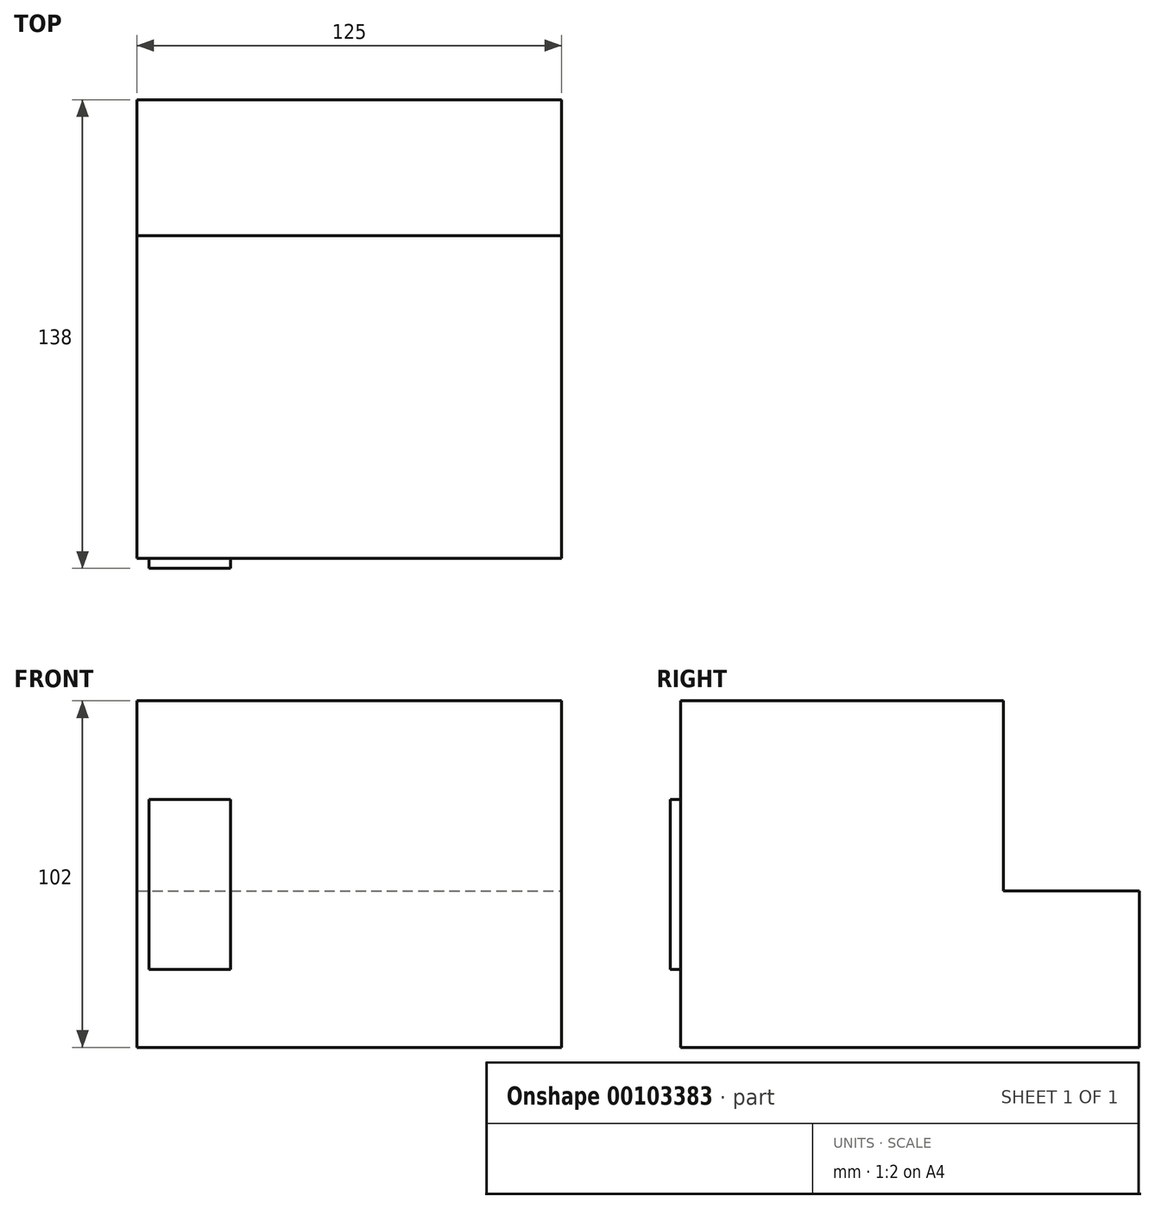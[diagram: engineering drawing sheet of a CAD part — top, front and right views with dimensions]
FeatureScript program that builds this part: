
annotation { "Feature Type Name" : "Feature", "Feature Type Description" : "" }
export const myFeature = defineFeature(function(context is Context, id is Id, definition is map)
    precondition{}
    {
        {
            var Q0;
            Q0=qCreatedBy(makeId("Top.planeOp"),FACE);
            var sketch = newSketch(context, id + "F0", { "sketchPlane" : qUnion([Q0])});
            skLineSegment(sketch, "E0.bottom", {"start": v(0, 0) * mm, "end": v(125, 0) * mm});
            skLineSegment(sketch, "E0.top", {"start": v(0, 135) * mm, "end": v(125, 135) * mm});
            skLineSegment(sketch, "E0.left", {"start": v(0, 0) * mm, "end": v(0, 135) * mm});
            skLineSegment(sketch, "E0.right", {"start": v(125, 0) * mm, "end": v(125, 135) * mm});
            skLineSegment(sketch, "E1", {"start": v(0, 95) * mm, "end": v(125, 95) * mm});
            skSolve(sketch);
        }
        {
            var Q0;
            Q0=qSketchRegion(id+"F0",true);
            var Q1;
            Q1=makeQuery(id+"F0.imprint","IMPRINT",FACE,{"disambiguationData":[TD([[makeQuery(id+"F0.imprint","IMPRINT",EDGE,{"derivedFrom":sQuery(id+"F0.wireOp",EDGE,"E0.bottom")}),1.0]])]});
            extrude(context, id + "F1", {"entities" : qUnion([Q0, Q1]), "depth" : 102 * mm});
        }
        {
            var Q0;
            {var subQ0=sQuery(id+"F0.wireOp",EDGE,"E0.top");Q0=makeQuery(id+"F0.imprint","IMPRINT",FACE,{"disambiguationData":[TD([[makeQuery(id+"F0.imprint","IMPRINT",EDGE,{"derivedFrom":subQ0}),-1.0]])]});}
            extrude(context, id + "F2", {"entities" : qUnion([Q0]), "operationType" : NewBodyOperationType.REMOVE, "depth" : 132.07 * mm, "hasSecondDirection" : true, "secondDirectionOppositeDirection" : false, "secondDirectionDepth" : 46 * mm});
        }
        {
            var Q0;
            Q0=makeQuery(id+"F1.opExtrude","SWEPT_FACE",FACE,{"disambiguationData":[OSD([sQuery(id+"F0.wireOp",EDGE,"E0.bottom")])]});
            var sketch = newSketch(context, id + "F3", { "sketchPlane" : qUnion([Q0])});
            skLineSegment(sketch, "E2.bottom", {"start": v(3.6, 73) * mm, "end": v(27.6, 73) * mm});
            skLineSegment(sketch, "E2.top", {"start": v(3.6, 23) * mm, "end": v(27.6, 23) * mm});
            skLineSegment(sketch, "E2.left", {"start": v(3.6, 73) * mm, "end": v(3.6, 23) * mm});
            skLineSegment(sketch, "E2.right", {"start": v(27.6, 73) * mm, "end": v(27.6, 23) * mm});
            skLineSegment(sketch, "E3", {"start": v(52.64, 95) * mm, "end": v(98.96, 95) * mm});
            skLineSegment(sketch, "E4", {"start": v(98.96, 95) * mm, "end": v(121, 65.28) * mm});
            skLineSegment(sketch, "E5", {"start": v(121, 65.28) * mm, "end": v(121, 27.36) * mm});
            skLineSegment(sketch, "E6", {"start": v(121, 27.36) * mm, "end": v(98.96, 7) * mm});
            skLineSegment(sketch, "E7", {"start": v(98.96, 7) * mm, "end": v(52.64, 7) * mm});
            skLineSegment(sketch, "E8", {"start": v(52.64, 7) * mm, "end": v(30.6, 27.36) * mm});
            skLineSegment(sketch, "E9", {"start": v(30.6, 27.36) * mm, "end": v(30.6, 65.28) * mm});
            skLineSegment(sketch, "E10", {"start": v(30.6, 65.28) * mm, "end": v(52.64, 95) * mm});
            skSolve(sketch);
        }
        {
            var Q0;
            Q0=makeQuery(id+"F3.imprint","IMPRINT",FACE,{"disambiguationData":[TD([[makeQuery(id+"F3.imprint","IMPRINT",EDGE,{"derivedFrom":sQuery(id+"F3.wireOp",EDGE,"E2.bottom")}),-1.0]])]});
            extrude(context, id + "F4", {"entities" : qUnion([Q0]), "operationType" : NewBodyOperationType.ADD, "depth" : 3 * mm});
        }
    });
